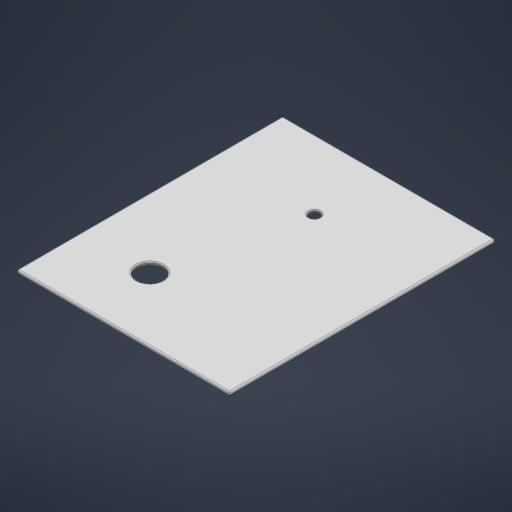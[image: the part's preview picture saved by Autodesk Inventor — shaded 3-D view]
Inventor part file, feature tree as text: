
AUTODESK INVENTOR PART (.ipt)
format: ipt  version: 2023 (Build 270158000, 158)  size: 207,872 bytes
history: native  units: mm
features: extrude x1, fillet x1, other x1
ambient origin geometry x8: Origin, YZ Plane, XZ Plane, XY Plane, X Axis, Y Axis, Z Axis, Center Point
bodies: Solid1 (feature_tree)
feature tree (3):
  extrude  "wire"  Depth=200.0mm
  fillet  "Fillet1"  Radius=250.0mm
  other  "page_lines"
